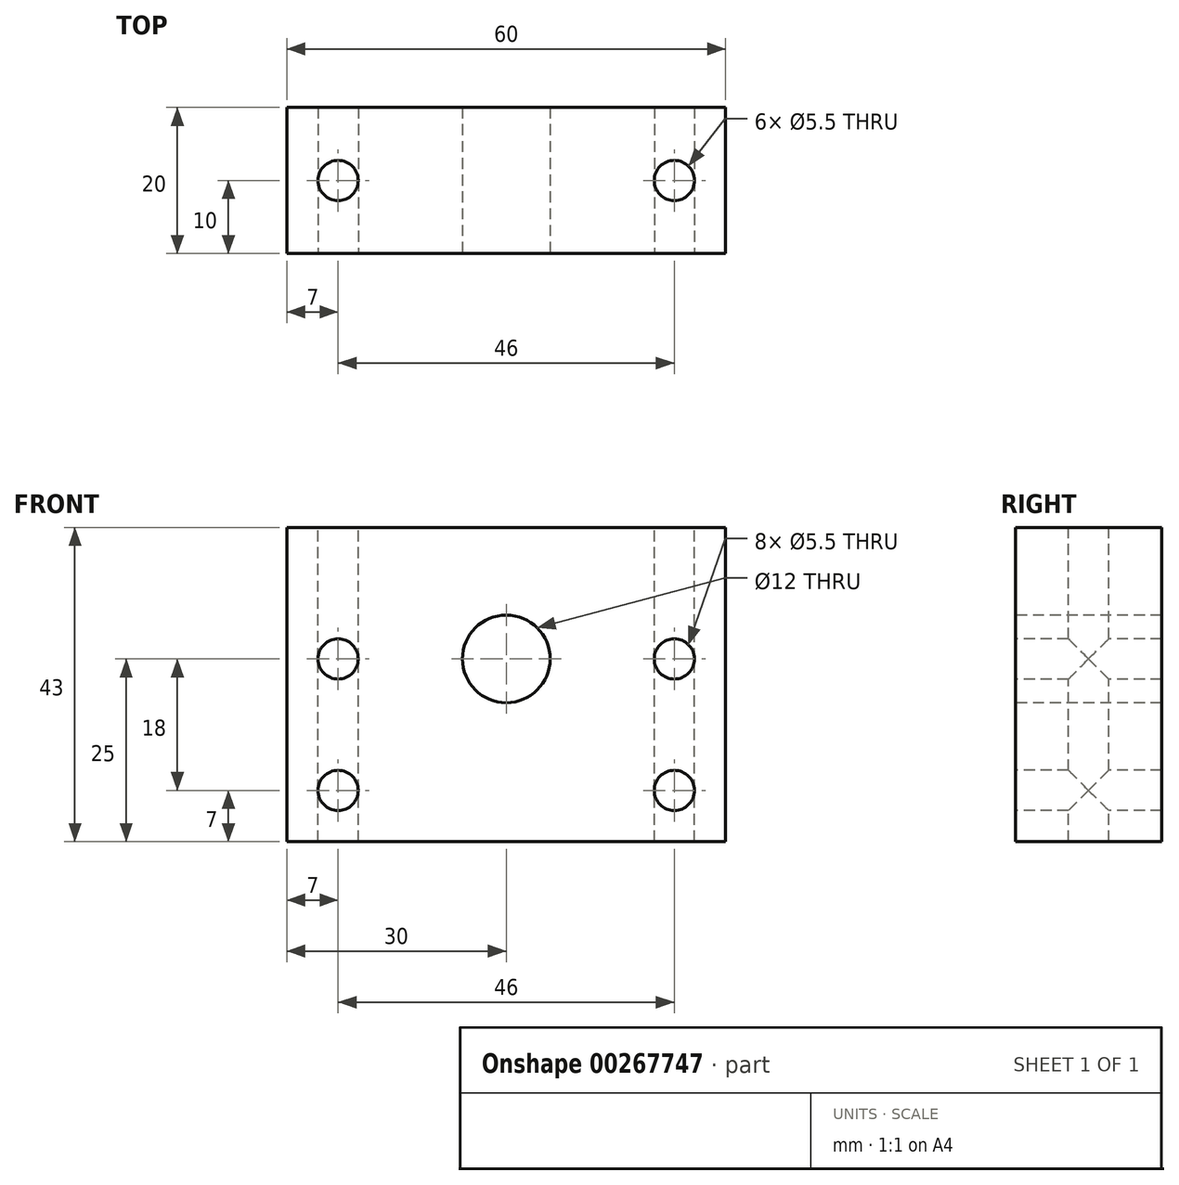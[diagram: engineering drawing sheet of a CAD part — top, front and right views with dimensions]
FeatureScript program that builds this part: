
annotation { "Feature Type Name" : "Feature", "Feature Type Description" : "" }
export const myFeature = defineFeature(function(context is Context, id is Id, definition is map)
    precondition{}
    {
        {
            var Q0;
            Q0=qCreatedBy(makeId("Front.planeOp"),FACE);
            var sketch = newSketch(context, id + "F0", { "sketchPlane" : qUnion([Q0])});
            skLineSegment(sketch, "E0.bottom", {"start": v(30, 21.5) * mm, "end": v(-30, 21.5) * mm});
            skLineSegment(sketch, "E0.top", {"start": v(30, -21.5) * mm, "end": v(-30, -21.5) * mm});
            skLineSegment(sketch, "E0.left", {"start": v(30, 21.5) * mm, "end": v(30, -21.5) * mm});
            skLineSegment(sketch, "E0.right", {"start": v(-30, 21.5) * mm, "end": v(-30, -21.5) * mm});
            skPoint(sketch, "E0.middle", {"position": v(0, 0) * mm});
            skLineSegment(sketch, "E1", {"start": v(0, -21.5) * mm, "end": v(0, 3.5) * mm, "construction": true});
            skPoint(sketch, "E1.endSnap0", {"position": v(0, -21.5) * mm});
            skCircle(sketch, "E2", {"center": v(0, 3.5) * mm, "radius": 6 * mm});
            skSolve(sketch);
        }
        {
            var Q0;
            Q0=qSketchRegion(id+"F0",true);
            extrude(context, id + "F1", {"entities" : qUnion([Q0]), "oppositeDirection" : true, "depth" : 20 * mm});
        }
        {
            var Q0;
            Q0=makeQuery(id+"F1.opExtrude","SWEPT_FACE",FACE,{"disambiguationData":[OSD([sQuery(id+"F0.wireOp",EDGE,"E0.bottom")])]});
            var sketch = newSketch(context, id + "F2", { "sketchPlane" : qUnion([Q0])});
            skLineSegment(sketch, "E3.bottom", {"start": v(23, 25) * mm, "end": v(-23, 25) * mm, "construction": true});
            skLineSegment(sketch, "E3.top", {"start": v(23, -25) * mm, "end": v(-23, -25) * mm, "construction": true});
            skLineSegment(sketch, "E3.left", {"start": v(23, 25) * mm, "end": v(23, -25) * mm, "construction": true});
            skLineSegment(sketch, "E3.right", {"start": v(-23, 25) * mm, "end": v(-23, -25) * mm, "construction": true});
            skPoint(sketch, "E3.middle", {"position": v(0, 0) * mm});
            skLineSegment(sketch, "E4", {"start": v(-30, 10) * mm, "end": v(30, 10) * mm, "construction": true});
            skCircle(sketch, "E5", {"center": v(-23, 10) * mm, "radius": 2.75 * mm});
            skCircle(sketch, "E6", {"center": v(23, 10) * mm, "radius": 2.75 * mm});
            skSolve(sketch);
        }
        {
            var Q0;
            Q0 = qSketchRegion(id + "F2", true);
            extrude(context, id + "F3", {"entities" : qUnion([Q0]), "operationType" : NewBodyOperationType.REMOVE, "endBound" : BoundingType.THROUGH_ALL, "oppositeDirection" : true, "depth" : 25 * mm});
        }
        {
            var Q0;
            Q0=makeQuery(id+"F1.opExtrude","CAP_FACE",FACE,{"disambiguationData":[OSD([sQuery(id+"F0.wireOp",EDGE,"E0.bottom"),sQuery(id+"F0.wireOp",EDGE,"E0.top"),sQuery(id+"F0.wireOp",EDGE,"E0.left"),sQuery(id+"F0.wireOp",EDGE,"E0.right"),sQuery(id+"F0.wireOp",EDGE,"E2")])],"isStart":true});
            var sketch = newSketch(context, id + "F4", { "sketchPlane" : qUnion([Q0])});
            skLineSegment(sketch, "E7", {"start": v(-30, -21.5) * mm, "end": v(-30, 3.5) * mm, "construction": true});
            skLineSegment(sketch, "E8", {"start": v(-30, 3.5) * mm, "end": v(30, 3.5) * mm, "construction": true});
            skCircle(sketch, "E9", {"center": v(-23, 3.5) * mm, "radius": 2.75 * mm});
            skCircle(sketch, "E10", {"center": v(23, 3.5) * mm, "radius": 2.75 * mm});
            skLineSegment(sketch, "E11", {"start": v(0, -21.5) * mm, "end": v(0, 21.5) * mm, "construction": true});
            skLineSegment(sketch, "E12", {"start": v(-30, 3.5) * mm, "end": v(-30, -14.5) * mm, "construction": true});
            skLineSegment(sketch, "E13", {"start": v(-30, -14.5) * mm, "end": v(30, -14.5) * mm, "construction": true});
            skCircle(sketch, "E14", {"center": v(-23, -14.5) * mm, "radius": 2.75 * mm});
            skCircle(sketch, "E15", {"center": v(23, -14.5) * mm, "radius": 2.75 * mm});
            skSolve(sketch);
        }
        {
            var Q0;
            Q0=makeQuery(id+"F4.imprint","IMPRINT",FACE,{"disambiguationData":[TD([[makeQuery(id+"F4.imprint","IMPRINT",EDGE,{"derivedFrom":sQuery(id+"F4.wireOp",EDGE,"E10")}),1.0]])]});
            var Q1;
            Q1=makeQuery(id+"F4.imprint","IMPRINT",FACE,{"disambiguationData":[TD([[makeQuery(id+"F4.imprint","IMPRINT",EDGE,{"derivedFrom":sQuery(id+"F4.wireOp",EDGE,"E14")}),1.0]])]});
            var Q2;
            Q2=makeQuery(id+"F4.imprint","IMPRINT",FACE,{"disambiguationData":[TD([[makeQuery(id+"F4.imprint","IMPRINT",EDGE,{"derivedFrom":sQuery(id+"F4.wireOp",EDGE,"E15")}),1.0]])]});
            var Q3;
            Q3=makeQuery(id+"F4.imprint","IMPRINT",FACE,{"disambiguationData":[TD([[makeQuery(id+"F4.imprint","IMPRINT",EDGE,{"derivedFrom":sQuery(id+"F4.wireOp",EDGE,"E9")}),1.0]])]});
            extrude(context, id + "F5", {"entities" : qUnion([Q0, Q1, Q2, Q3]), "operationType" : NewBodyOperationType.REMOVE, "endBound" : BoundingType.THROUGH_ALL, "oppositeDirection" : true, "depth" : 25 * mm});
        }
    });
